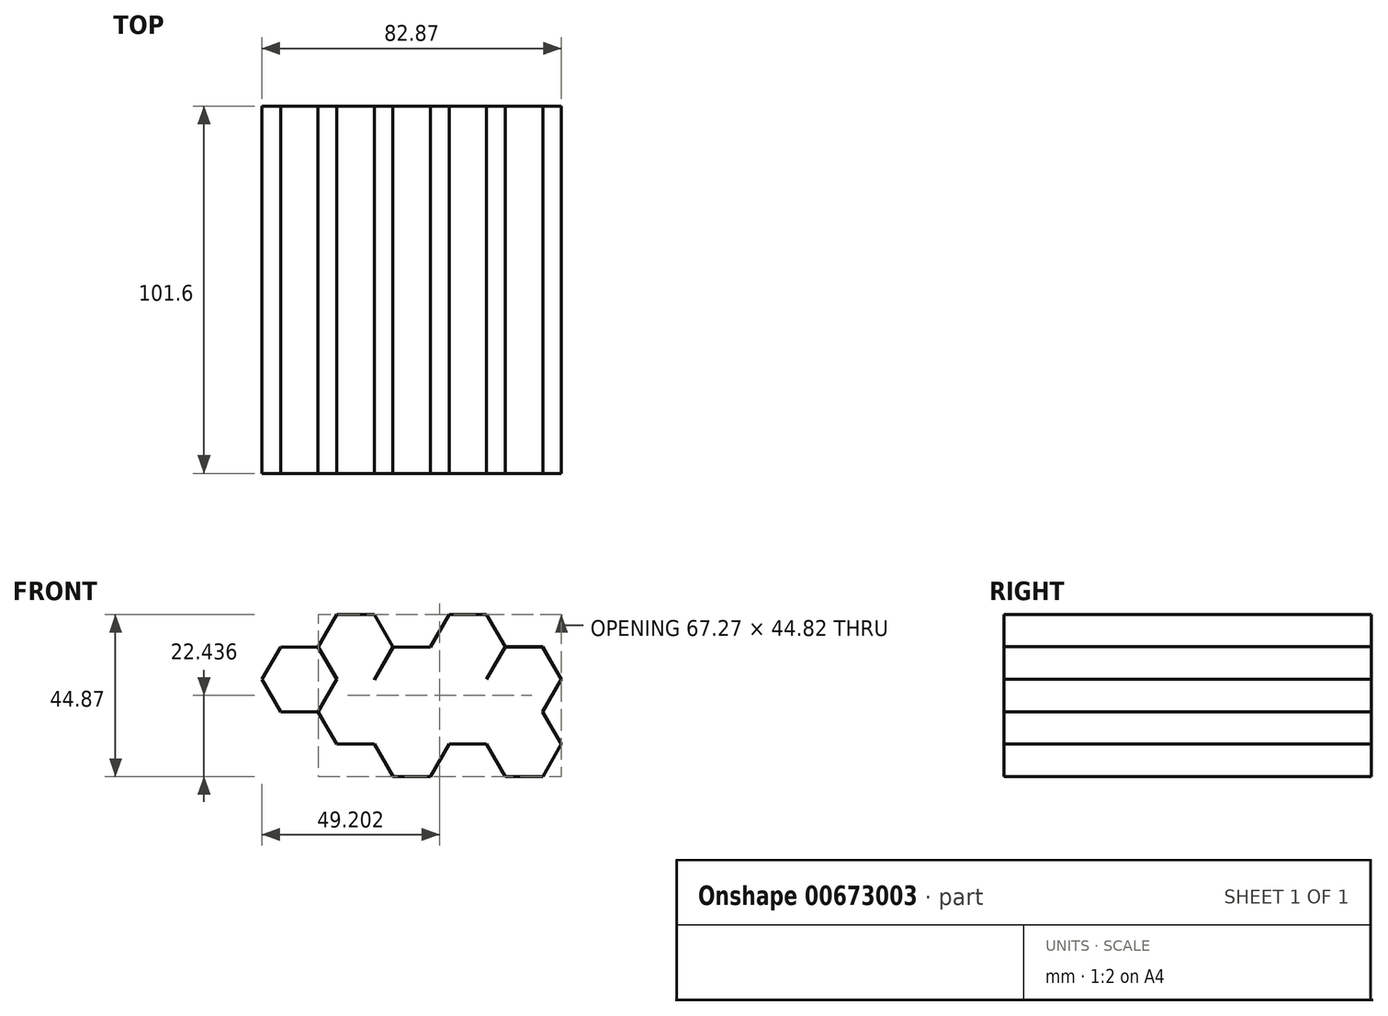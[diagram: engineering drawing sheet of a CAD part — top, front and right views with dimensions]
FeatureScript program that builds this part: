
annotation { "Feature Type Name" : "Feature", "Feature Type Description" : "" }
export const myFeature = defineFeature(function(context is Context, id is Id, definition is map)
    precondition{}
    {
        {
            var Q0;
            Q0=qCreatedBy(makeId("Front.planeOp"),FACE);
            var sketch = newSketch(context, id + "F0", { "sketchPlane" : qUnion([Q0])});
            skCircle(sketch, "E0.cCircle", {"center": v(0, 0) * mm, "radius": 8.98 * mm, "construction": true});
            skLineSegment(sketch, "E0.0", {"start": v(-5.18, 8.98) * mm, "end": v(5.18, 8.98) * mm});
            skLineSegment(sketch, "E0.1", {"start": v(5.18, 8.98) * mm, "end": v(10.37, 0) * mm});
            skLineSegment(sketch, "E0.2", {"start": v(10.37, 0) * mm, "end": v(5.18, -8.98) * mm});
            skLineSegment(sketch, "E0.3", {"start": v(5.18, -8.98) * mm, "end": v(-5.18, -8.98) * mm});
            skLineSegment(sketch, "E0.4", {"start": v(-5.18, -8.98) * mm, "end": v(-10.37, 0) * mm});
            skLineSegment(sketch, "E0.5", {"start": v(-10.37, 0) * mm, "end": v(-5.18, 8.98) * mm});
            skPoint(sketch, "E0.0.midPoint", {"position": v(0, 8.98) * mm});
            skCircle(sketch, "E1.cCircle", {"center": v(0, 17.94) * mm, "radius": 8.97 * mm, "construction": true});
            skLineSegment(sketch, "E1.0", {"start": v(5.17, 26.91) * mm, "end": v(10.35, 17.95) * mm});
            skLineSegment(sketch, "E1.1", {"start": v(10.35, 17.95) * mm, "end": v(5.18, 8.98) * mm});
            skLineSegment(sketch, "E1.2", {"start": v(5.18, 8.98) * mm, "end": v(-5.17, 8.97) * mm});
            skLineSegment(sketch, "E1.3", {"start": v(-5.17, 8.97) * mm, "end": v(-10.35, 17.93) * mm});
            skLineSegment(sketch, "E1.4", {"start": v(-10.35, 17.93) * mm, "end": v(-5.18, 26.9) * mm});
            skLineSegment(sketch, "E1.5", {"start": v(-5.18, 26.9) * mm, "end": v(5.17, 26.91) * mm});
            skPoint(sketch, "E1.0.midPoint", {"position": v(7.76, 22.43) * mm});
            skCircle(sketch, "E2.cCircle", {"center": v(-15.54, 8.97) * mm, "radius": 8.98 * mm, "construction": true});
            skLineSegment(sketch, "E2.0", {"start": v(-20.72, 17.95) * mm, "end": v(-10.35, 17.95) * mm});
            skLineSegment(sketch, "E2.1", {"start": v(-10.35, 17.95) * mm, "end": v(-5.17, 8.97) * mm});
            skLineSegment(sketch, "E2.2", {"start": v(-5.17, 8.97) * mm, "end": v(-10.35, 0) * mm});
            skLineSegment(sketch, "E2.3", {"start": v(-10.35, 0) * mm, "end": v(-20.72, 0) * mm});
            skLineSegment(sketch, "E2.4", {"start": v(-20.72, 0) * mm, "end": v(-25.9, 8.97) * mm});
            skLineSegment(sketch, "E2.5", {"start": v(-25.9, 8.97) * mm, "end": v(-20.72, 17.95) * mm});
            skPoint(sketch, "E2.0.midPoint", {"position": v(-15.54, 17.95) * mm});
            skCircle(sketch, "E3.cCircle", {"center": v(-15.54, 26.91) * mm, "radius": 8.97 * mm, "construction": true});
            skLineSegment(sketch, "E3.0", {"start": v(-10.37, 35.88) * mm, "end": v(-5.18, 26.92) * mm});
            skLineSegment(sketch, "E3.1", {"start": v(-5.18, 26.92) * mm, "end": v(-10.35, 17.95) * mm});
            skLineSegment(sketch, "E3.2", {"start": v(-10.35, 17.95) * mm, "end": v(-20.7, 17.94) * mm});
            skLineSegment(sketch, "E3.3", {"start": v(-20.7, 17.94) * mm, "end": v(-25.9, 26.9) * mm});
            skLineSegment(sketch, "E3.4", {"start": v(-25.9, 26.9) * mm, "end": v(-20.72, 35.88) * mm});
            skLineSegment(sketch, "E3.5", {"start": v(-20.72, 35.88) * mm, "end": v(-10.37, 35.88) * mm});
            skPoint(sketch, "E3.0.midPoint", {"position": v(-7.78, 31.4) * mm});
            skCircle(sketch, "E4.cCircle", {"center": v(15.52, 8.98) * mm, "radius": 8.98 * mm, "construction": true});
            skLineSegment(sketch, "E4.0", {"start": v(10.34, 17.96) * mm, "end": v(20.7, 17.96) * mm});
            skLineSegment(sketch, "E4.1", {"start": v(20.7, 17.96) * mm, "end": v(25.9, 8.98) * mm});
            skLineSegment(sketch, "E4.2", {"start": v(25.9, 8.98) * mm, "end": v(20.7, 0) * mm});
            skLineSegment(sketch, "E4.3", {"start": v(20.7, 0) * mm, "end": v(10.34, 0) * mm});
            skLineSegment(sketch, "E4.4", {"start": v(10.34, 0) * mm, "end": v(5.16, 8.98) * mm});
            skLineSegment(sketch, "E4.5", {"start": v(5.16, 8.98) * mm, "end": v(10.34, 17.96) * mm});
            skPoint(sketch, "E4.0.midPoint", {"position": v(15.52, 17.96) * mm});
            skCircle(sketch, "E5.cCircle", {"center": v(15.52, 26.92) * mm, "radius": 8.97 * mm, "construction": true});
            skLineSegment(sketch, "E5.0", {"start": v(20.7, 35.89) * mm, "end": v(25.88, 26.93) * mm});
            skLineSegment(sketch, "E5.1", {"start": v(25.88, 26.93) * mm, "end": v(20.7, 17.96) * mm});
            skLineSegment(sketch, "E5.2", {"start": v(20.7, 17.96) * mm, "end": v(10.35, 17.95) * mm});
            skLineSegment(sketch, "E5.3", {"start": v(10.35, 17.95) * mm, "end": v(5.17, 26.91) * mm});
            skLineSegment(sketch, "E5.4", {"start": v(5.17, 26.91) * mm, "end": v(10.34, 35.88) * mm});
            skLineSegment(sketch, "E5.5", {"start": v(10.34, 35.88) * mm, "end": v(20.7, 35.89) * mm});
            skPoint(sketch, "E5.0.midPoint", {"position": v(23.29, 31.4) * mm});
            skCircle(sketch, "E6.cCircle", {"center": v(31.06, 0) * mm, "radius": 8.98 * mm, "construction": true});
            skLineSegment(sketch, "E6.0", {"start": v(25.88, 8.99) * mm, "end": v(36.25, 8.99) * mm});
            skLineSegment(sketch, "E6.1", {"start": v(36.25, 8.99) * mm, "end": v(41.43, 0) * mm});
            skLineSegment(sketch, "E6.2", {"start": v(41.43, 0) * mm, "end": v(36.25, -8.97) * mm});
            skLineSegment(sketch, "E6.3", {"start": v(36.25, -8.97) * mm, "end": v(25.88, -8.97) * mm});
            skLineSegment(sketch, "E6.4", {"start": v(25.88, -8.97) * mm, "end": v(20.7, 0) * mm});
            skLineSegment(sketch, "E6.5", {"start": v(20.7, 0) * mm, "end": v(25.88, 8.99) * mm});
            skPoint(sketch, "E6.0.midPoint", {"position": v(31.06, 8.99) * mm});
            skCircle(sketch, "E7.cCircle", {"center": v(31.06, 17.95) * mm, "radius": 8.97 * mm, "construction": true});
            skLineSegment(sketch, "E7.0", {"start": v(36.23, 26.92) * mm, "end": v(41.42, 17.96) * mm});
            skLineSegment(sketch, "E7.1", {"start": v(41.42, 17.96) * mm, "end": v(36.25, 8.99) * mm});
            skLineSegment(sketch, "E7.2", {"start": v(36.25, 8.99) * mm, "end": v(25.9, 8.98) * mm});
            skLineSegment(sketch, "E7.3", {"start": v(25.9, 8.98) * mm, "end": v(20.7, 17.94) * mm});
            skLineSegment(sketch, "E7.4", {"start": v(20.7, 17.94) * mm, "end": v(25.88, 26.91) * mm});
            skLineSegment(sketch, "E7.5", {"start": v(25.88, 26.91) * mm, "end": v(36.23, 26.92) * mm});
            skPoint(sketch, "E7.0.midPoint", {"position": v(38.82, 22.44) * mm});
            skCircle(sketch, "E8.cCircle", {"center": v(-31.09, 0) * mm, "radius": 8.98 * mm, "construction": true});
            skLineSegment(sketch, "E8.0", {"start": v(-36.27, 8.97) * mm, "end": v(-25.9, 8.97) * mm});
            skLineSegment(sketch, "E8.1", {"start": v(-25.9, 8.97) * mm, "end": v(-20.72, 0) * mm});
            skLineSegment(sketch, "E8.2", {"start": v(-20.72, 0) * mm, "end": v(-25.9, -8.99) * mm});
            skLineSegment(sketch, "E8.3", {"start": v(-25.9, -8.99) * mm, "end": v(-36.27, -8.99) * mm});
            skLineSegment(sketch, "E8.4", {"start": v(-36.27, -8.99) * mm, "end": v(-41.45, 0) * mm});
            skLineSegment(sketch, "E8.5", {"start": v(-41.45, 0) * mm, "end": v(-36.27, 8.97) * mm});
            skPoint(sketch, "E8.0.midPoint", {"position": v(-31.09, 8.97) * mm});
            skCircle(sketch, "E9.cCircle", {"center": v(-31.09, 17.93) * mm, "radius": 8.97 * mm, "construction": true});
            skLineSegment(sketch, "E9.0", {"start": v(-25.92, 26.9) * mm, "end": v(-20.73, 17.94) * mm});
            skLineSegment(sketch, "E9.1", {"start": v(-20.73, 17.94) * mm, "end": v(-25.9, 8.97) * mm});
            skLineSegment(sketch, "E9.2", {"start": v(-25.9, 8.97) * mm, "end": v(-36.26, 8.96) * mm});
            skLineSegment(sketch, "E9.3", {"start": v(-36.26, 8.96) * mm, "end": v(-41.44, 17.93) * mm});
            skLineSegment(sketch, "E9.4", {"start": v(-41.44, 17.93) * mm, "end": v(-36.27, 26.9) * mm});
            skLineSegment(sketch, "E9.5", {"start": v(-36.27, 26.9) * mm, "end": v(-25.92, 26.9) * mm});
            skPoint(sketch, "E9.0.midPoint", {"position": v(-23.33, 22.42) * mm});
            skSolve(sketch);
        }
        {
            var Q0;
            {var subQ6=sQuery(id+"F0.wireOp",EDGE,"E0.1");Q0=makeQuery(id+"F0.imprint","IMPRINT",FACE,{"disambiguationData":[TD([[makeQuery(id+"F0.imprint","IMPRINT",EDGE,{"derivedFrom":subQ6}),1.0]])]});}
            var Q1;
            {var subQ8=sQuery(id+"F0.wireOp",EDGE,"E0.2");Q1=makeQuery(id+"F0.imprint","IMPRINT",FACE,{"disambiguationData":[TD([[makeQuery(id+"F0.imprint","IMPRINT",EDGE,{"derivedFrom":subQ8}),-1.0]])]});}
            var Q2;
            Q2=makeQuery(id+"F0.imprint","IMPRINT",FACE,{"disambiguationData":[TD([[makeQuery(id+"F0.imprint","IMPRINT",EDGE,{"derivedFrom":sQuery(id+"F0.wireOp",EDGE,"E9.0")}),-1.0]])]});
            var Q3;
            Q3=makeQuery(id+"F0.imprint","IMPRINT",FACE,{"disambiguationData":[TD([[makeQuery(id+"F0.imprint","IMPRINT",EDGE,{"derivedFrom":sQuery(id+"F0.wireOp",EDGE,"E7.0")}),-1.0]])]});
            var Q4;
            {var subQ1=sQuery(id+"F0.wireOp",EDGE,"E4.2");Q4=makeQuery(id+"F0.imprint","IMPRINT",FACE,{"disambiguationData":[TD([[makeQuery(id+"F0.imprint","IMPRINT",EDGE,{"derivedFrom":subQ1}),1.0]])]});}
            var Q5;
            Q5=makeQuery(id+"F0.imprint","IMPRINT",FACE,{"disambiguationData":[TD([[makeQuery(id+"F0.imprint","IMPRINT",EDGE,{"derivedFrom":sQuery(id+"F0.wireOp",EDGE,"E8.1")}),-1.0]])]});
            var Q6;
            {var subQ5=sQuery(id+"F0.wireOp",EDGE,"E0.5");Q6=makeQuery(id+"F0.imprint","IMPRINT",FACE,{"disambiguationData":[TD([[makeQuery(id+"F0.imprint","IMPRINT",EDGE,{"derivedFrom":subQ5}),1.0]])]});}
            var Q7;
            {var subQ0=sQuery(id+"F0.wireOp",EDGE,"E1.5");Q7=makeQuery(id+"F0.imprint","IMPRINT",FACE,{"disambiguationData":[TD([[makeQuery(id+"F0.imprint","IMPRINT",EDGE,{"derivedFrom":subQ0}),-1.0]])]});}
            var Q8;
            {var subQ5=sQuery(id+"F0.wireOp",EDGE,"E1.1");Q8=makeQuery(id+"F0.imprint","IMPRINT",FACE,{"disambiguationData":[TD([[makeQuery(id+"F0.imprint","IMPRINT",EDGE,{"derivedFrom":subQ5}),-1.0]])]});}
            var Q9;
            {var subQ7=sQuery(id+"F0.wireOp",EDGE,"E4.2");Q9=makeQuery(id+"F0.imprint","IMPRINT",FACE,{"disambiguationData":[TD([[makeQuery(id+"F0.imprint","IMPRINT",EDGE,{"derivedFrom":subQ7}),-1.0]])]});}
            var Q10;
            {var subQ0=sQuery(id+"F0.wireOp",EDGE,"E3.2");Q10=makeQuery(id+"F0.imprint","IMPRINT",FACE,{"disambiguationData":[TD([[makeQuery(id+"F0.imprint","IMPRINT",EDGE,{"derivedFrom":subQ0}),-1.0]])]});}
            var Q11;
            {var subQ4=sQuery(id+"F0.wireOp",EDGE,"E0.5");Q11=makeQuery(id+"F0.imprint","IMPRINT",FACE,{"disambiguationData":[TD([[makeQuery(id+"F0.imprint","IMPRINT",EDGE,{"derivedFrom":subQ4}),-1.0]])]});}
            var Q12;
            {var subQ0=sQuery(id+"F0.wireOp",EDGE,"E1.2");var subQ3=sQuery(id+"F0.wireOp",EDGE,"E2.1");var subQ5=makeQuery(id+"F0.imprint","INTERSECT",VERTEX,{"derivedFrom":[subQ0,subQ3,sQuery(id+"F0.wireOp",EDGE,"E2.2")]});Q12=makeQuery(id+"F0.imprint","IMPRINT",FACE,{"disambiguationData":[TD([[makeQuery(id+"F0.imprint","IMPRINT",EDGE,{"disambiguationData":[TD([[subQ5,1.0]])],"derivedFrom":subQ3}),1.0]])]});}
            var Q13;
            {var subQ0=sQuery(id+"F0.wireOp",EDGE,"E0.1");Q13=makeQuery(id+"F0.imprint","IMPRINT",FACE,{"disambiguationData":[TD([[makeQuery(id+"F0.imprint","IMPRINT",EDGE,{"derivedFrom":subQ0}),-1.0]])]});}
            var Q14;
            {var subQ0=sQuery(id+"F0.wireOp",EDGE,"E5.2");Q14=makeQuery(id+"F0.imprint","IMPRINT",FACE,{"disambiguationData":[TD([[makeQuery(id+"F0.imprint","IMPRINT",EDGE,{"derivedFrom":subQ0}),-1.0]])]});}
            var Q15;
            {var subQ3=sQuery(id+"F0.wireOp",EDGE,"E7.2");Q15=makeQuery(id+"F0.imprint","IMPRINT",FACE,{"disambiguationData":[TD([[makeQuery(id+"F0.imprint","IMPRINT",EDGE,{"derivedFrom":subQ3}),-1.0]])]});}
            var Q16;
            {var subQ0=sQuery(id+"F0.wireOp",EDGE,"E1.3");Q16=makeQuery(id+"F0.imprint","IMPRINT",FACE,{"disambiguationData":[TD([[makeQuery(id+"F0.imprint","IMPRINT",EDGE,{"derivedFrom":subQ0}),-1.0]])]});}
            var Q17;
            {var subQ0=sQuery(id+"F0.wireOp",EDGE,"E7.3");var subQ3=sQuery(id+"F0.wireOp",EDGE,"E7.4");var subQ5=makeQuery(id+"F0.imprint","INTERSECT",VERTEX,{"derivedFrom":[subQ0,subQ3]});Q17=makeQuery(id+"F0.imprint","IMPRINT",FACE,{"disambiguationData":[TD([[makeQuery(id+"F0.imprint","IMPRINT",EDGE,{"disambiguationData":[TD([[subQ5,-1.0]])],"derivedFrom":subQ3}),-1.0]])]});}
            var Q18;
            {var subQ0=sQuery(id+"F0.wireOp",EDGE,"E9.2");Q18=makeQuery(id+"F0.imprint","IMPRINT",FACE,{"disambiguationData":[TD([[makeQuery(id+"F0.imprint","IMPRINT",EDGE,{"derivedFrom":subQ0}),-1.0]])]});}
            var Q19;
            Q19=makeQuery(id+"F0.imprint","IMPRINT",FACE,{"disambiguationData":[TD([[makeQuery(id+"F0.imprint","IMPRINT",EDGE,{"derivedFrom":sQuery(id+"F0.wireOp",EDGE,"E3.0")}),-1.0]])]});
            var Q20;
            Q20=makeQuery(id+"F0.imprint","IMPRINT",FACE,{"disambiguationData":[TD([[makeQuery(id+"F0.imprint","IMPRINT",EDGE,{"derivedFrom":sQuery(id+"F0.wireOp",EDGE,"E5.0")}),-1.0]])]});
            extrude(context, id + "F1", {"entities" : qUnion([Q0, Q1, Q2, Q3, Q4, Q5, Q6, Q7, Q8, Q9, Q10, Q11, Q12, Q13, Q14, Q15, Q16, Q17, Q18, Q19, Q20]), "depth" : 101.6 * mm, "offsetDistance" : 25.4 * mm});
        }
        {
            var Q0;
            Q0=makeQuery(id+"F1.opExtrude","CAP_FACE",FACE,{"disambiguationData":[OSD([sQuery(id+"F0.wireOp",EDGE,"E0.2"),sQuery(id+"F0.wireOp",EDGE,"E0.3"),sQuery(id+"F0.wireOp",EDGE,"E0.4"),sQuery(id+"F0.wireOp",EDGE,"E1.4"),sQuery(id+"F0.wireOp",EDGE,"E1.5"),sQuery(id+"F0.wireOp",EDGE,"E2.0"),sQuery(id+"F0.wireOp",EDGE,"E2.1"),sQuery(id+"F0.wireOp",EDGE,"E2.3"),sQuery(id+"F0.wireOp",EDGE,"E2.5"),sQuery(id+"F0.wireOp",EDGE,"E3.0"),sQuery(id+"F0.wireOp",EDGE,"E3.1"),sQuery(id+"F0.wireOp",EDGE,"E3.3"),sQuery(id+"F0.wireOp",EDGE,"E3.4"),sQuery(id+"F0.wireOp",EDGE,"E3.5"),sQuery(id+"F0.wireOp",EDGE,"E4.1"),sQuery(id+"F0.wireOp",EDGE,"E4.3"),sQuery(id+"F0.wireOp",EDGE,"E5.0"),sQuery(id+"F0.wireOp",EDGE,"E5.1"),sQuery(id+"F0.wireOp",EDGE,"E5.4"),sQuery(id+"F0.wireOp",EDGE,"E5.5"),sQuery(id+"F0.wireOp",EDGE,"E6.1"),sQuery(id+"F0.wireOp",EDGE,"E6.2"),sQuery(id+"F0.wireOp",EDGE,"E6.3"),sQuery(id+"F0.wireOp",EDGE,"E6.4"),sQuery(id+"F0.wireOp",EDGE,"E7.0"),sQuery(id+"F0.wireOp",EDGE,"E7.1"),sQuery(id+"F0.wireOp",EDGE,"E7.4"),sQuery(id+"F0.wireOp",EDGE,"E7.5"),sQuery(id+"F0.wireOp",EDGE,"E8.0"),sQuery(id+"F0.wireOp",EDGE,"E8.2"),sQuery(id+"F0.wireOp",EDGE,"E8.3"),sQuery(id+"F0.wireOp",EDGE,"E8.4"),sQuery(id+"F0.wireOp",EDGE,"E8.5"),sQuery(id+"F0.wireOp",EDGE,"E9.0"),sQuery(id+"F0.wireOp",EDGE,"E9.1"),sQuery(id+"F0.wireOp",EDGE,"E9.3"),sQuery(id+"F0.wireOp",EDGE,"E9.4"),sQuery(id+"F0.wireOp",EDGE,"E9.5")])],"isStart":true});
            var Q1;
            Q1=makeQuery(id+"F1.opExtrude","CAP_FACE",FACE,{"disambiguationData":[OSD([sQuery(id+"F0.wireOp",EDGE,"E0.2"),sQuery(id+"F0.wireOp",EDGE,"E0.3"),sQuery(id+"F0.wireOp",EDGE,"E0.4"),sQuery(id+"F0.wireOp",EDGE,"E1.4"),sQuery(id+"F0.wireOp",EDGE,"E1.5"),sQuery(id+"F0.wireOp",EDGE,"E2.0"),sQuery(id+"F0.wireOp",EDGE,"E2.1"),sQuery(id+"F0.wireOp",EDGE,"E2.3"),sQuery(id+"F0.wireOp",EDGE,"E2.5"),sQuery(id+"F0.wireOp",EDGE,"E3.0"),sQuery(id+"F0.wireOp",EDGE,"E3.1"),sQuery(id+"F0.wireOp",EDGE,"E3.3"),sQuery(id+"F0.wireOp",EDGE,"E3.4"),sQuery(id+"F0.wireOp",EDGE,"E3.5"),sQuery(id+"F0.wireOp",EDGE,"E4.1"),sQuery(id+"F0.wireOp",EDGE,"E4.3"),sQuery(id+"F0.wireOp",EDGE,"E5.0"),sQuery(id+"F0.wireOp",EDGE,"E5.1"),sQuery(id+"F0.wireOp",EDGE,"E5.4"),sQuery(id+"F0.wireOp",EDGE,"E5.5"),sQuery(id+"F0.wireOp",EDGE,"E6.1"),sQuery(id+"F0.wireOp",EDGE,"E6.2"),sQuery(id+"F0.wireOp",EDGE,"E6.3"),sQuery(id+"F0.wireOp",EDGE,"E6.4"),sQuery(id+"F0.wireOp",EDGE,"E7.0"),sQuery(id+"F0.wireOp",EDGE,"E7.1"),sQuery(id+"F0.wireOp",EDGE,"E7.4"),sQuery(id+"F0.wireOp",EDGE,"E7.5"),sQuery(id+"F0.wireOp",EDGE,"E8.0"),sQuery(id+"F0.wireOp",EDGE,"E8.2"),sQuery(id+"F0.wireOp",EDGE,"E8.3"),sQuery(id+"F0.wireOp",EDGE,"E8.4"),sQuery(id+"F0.wireOp",EDGE,"E8.5"),sQuery(id+"F0.wireOp",EDGE,"E9.0"),sQuery(id+"F0.wireOp",EDGE,"E9.1"),sQuery(id+"F0.wireOp",EDGE,"E9.3"),sQuery(id+"F0.wireOp",EDGE,"E9.4"),sQuery(id+"F0.wireOp",EDGE,"E9.5")])],"isStart":false});
            shell(context, id + "F2", {"entities" : qUnion([Q0, Q1]), "thickness" : 0.03 * mm});
        }
        {
            var Q0;
            Q0=makeQuery(id+"F1.opExtrude","CAP_FACE",FACE,{"disambiguationData":[OSD([sQuery(id+"F0.wireOp",EDGE,"E0.2"),sQuery(id+"F0.wireOp",EDGE,"E0.3"),sQuery(id+"F0.wireOp",EDGE,"E0.4"),sQuery(id+"F0.wireOp",EDGE,"E1.4"),sQuery(id+"F0.wireOp",EDGE,"E1.5"),sQuery(id+"F0.wireOp",EDGE,"E2.0"),sQuery(id+"F0.wireOp",EDGE,"E2.1"),sQuery(id+"F0.wireOp",EDGE,"E2.3"),sQuery(id+"F0.wireOp",EDGE,"E2.5"),sQuery(id+"F0.wireOp",EDGE,"E3.0"),sQuery(id+"F0.wireOp",EDGE,"E3.1"),sQuery(id+"F0.wireOp",EDGE,"E3.3"),sQuery(id+"F0.wireOp",EDGE,"E3.4"),sQuery(id+"F0.wireOp",EDGE,"E3.5"),sQuery(id+"F0.wireOp",EDGE,"E4.1"),sQuery(id+"F0.wireOp",EDGE,"E4.3"),sQuery(id+"F0.wireOp",EDGE,"E5.0"),sQuery(id+"F0.wireOp",EDGE,"E5.1"),sQuery(id+"F0.wireOp",EDGE,"E5.4"),sQuery(id+"F0.wireOp",EDGE,"E5.5"),sQuery(id+"F0.wireOp",EDGE,"E6.1"),sQuery(id+"F0.wireOp",EDGE,"E6.2"),sQuery(id+"F0.wireOp",EDGE,"E6.3"),sQuery(id+"F0.wireOp",EDGE,"E6.4"),sQuery(id+"F0.wireOp",EDGE,"E7.0"),sQuery(id+"F0.wireOp",EDGE,"E7.1"),sQuery(id+"F0.wireOp",EDGE,"E7.4"),sQuery(id+"F0.wireOp",EDGE,"E7.5"),sQuery(id+"F0.wireOp",EDGE,"E8.0"),sQuery(id+"F0.wireOp",EDGE,"E8.2"),sQuery(id+"F0.wireOp",EDGE,"E8.3"),sQuery(id+"F0.wireOp",EDGE,"E8.4"),sQuery(id+"F0.wireOp",EDGE,"E8.5"),sQuery(id+"F0.wireOp",EDGE,"E9.0"),sQuery(id+"F0.wireOp",EDGE,"E9.1"),sQuery(id+"F0.wireOp",EDGE,"E9.3"),sQuery(id+"F0.wireOp",EDGE,"E9.4"),sQuery(id+"F0.wireOp",EDGE,"E9.5")])],"isStart":true});
            var sketch = newSketch(context, id + "F3", { "sketchPlane" : qUnion([Q0])});
            skLineSegment(sketch, "E10", {"start": v(10.38, 17.95) * mm, "end": v(20.7, 17.92) * mm});
            skLineSegment(sketch, "E11", {"start": v(36.27, 8.97) * mm, "end": v(25.9, 8.97) * mm});
            skLineSegment(sketch, "E12", {"start": v(25.9, 8.97) * mm, "end": v(20.74, 0.02) * mm});
            skLineSegment(sketch, "E13", {"start": v(-36.22, 8.99) * mm, "end": v(-25.88, 8.99) * mm});
            skLineSegment(sketch, "E14", {"start": v(-25.88, 8.99) * mm, "end": v(-20.7, 0) * mm});
            skLineSegment(sketch, "E15", {"start": v(5.2, 8.97) * mm, "end": v(10.36, 0) * mm});
            skLineSegment(sketch, "E16", {"start": v(10.38, 17.95) * mm, "end": v(5.2, 8.97) * mm});
            skLineSegment(sketch, "E17", {"start": v(5.2, 8.97) * mm, "end": v(-5.17, 8.97) * mm});
            skLineSegment(sketch, "E18", {"start": v(-5.17, 8.97) * mm, "end": v(-10.35, 0.03) * mm});
            skLineSegment(sketch, "E19", {"start": v(-20.68, 17.96) * mm, "end": v(-25.88, 8.99) * mm});
            skLineSegment(sketch, "E20", {"start": v(-20.71, 17.9) * mm, "end": v(-10.35, 17.9) * mm});
            skLineSegment(sketch, "E21", {"start": v(-10.35, 17.9) * mm, "end": v(-5.17, 8.97) * mm});
            skLineSegment(sketch, "E22", {"start": v(-5.17, 26.91) * mm, "end": v(-10.35, 17.9) * mm});
            skSolve(sketch);
        }
        {
            var Q0;
            Q0=sQuery(id+"F3.wireOp",EDGE,"E20");
            var Q1;
            Q1=sQuery(id+"F3.wireOp",EDGE,"E22");
            var Q2;
            Q2=sQuery(id+"F3.wireOp",EDGE,"E19");
            var Q3;
            Q3=sQuery(id+"F3.wireOp",EDGE,"E14");
            var Q4;
            Q4=sQuery(id+"F3.wireOp",EDGE,"E12");
            var Q5;
            Q5=sQuery(id+"F3.wireOp",EDGE,"E15");
            var Q6;
            Q6=sQuery(id+"F3.wireOp",EDGE,"E18");
            var Q7;
            Q7=sQuery(id+"F3.wireOp",EDGE,"E16");
            extrude(context, id + "F4", {"bodyType" : ToolBodyType.SURFACE, "surfaceEntities" : qUnion([Q0, Q1, Q2, Q3, Q4, Q5, Q6, Q7]), "oppositeDirection" : true, "depth" : 101.6 * mm, "offsetDistance" : 25.4 * mm});
        }
    });
